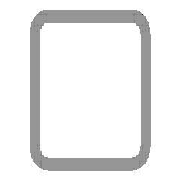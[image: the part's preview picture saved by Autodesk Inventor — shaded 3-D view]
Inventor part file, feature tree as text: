
AUTODESK INVENTOR PART (.ipt)
format: ipt  version: 2025 (Build 290162010, 162A)  size: 134,656 bytes
history: native  units: mm (DEFAULTED — no unit token found)
features: other x4, sketch x1, plane x1
ambient origin geometry x8: Origin, YZ Plane, XZ Plane, XY Plane, X Axis, Y Axis, Z Axis, Center Point
bodies: Solid1 (feature_tree), Body (feature_tree)
feature tree (6):
  parser-record x1  (decoder bookkeeping rows leaked as tree rows — omitted from the tree; the rows remain in map.json)
  other  "Driven Length"
  other  "Start Plane"
  other  "End Plane"
  sketch  "Sketch3"  dims[d3=2200.0mm d4=0.0mm d7=6.0mm d9=100.0mm d11=100.0mm d12=3.0mm d13=-0.0mm d14=2200.0mm d15=50.0mm d16=50.0mm d17=90.0deg d18=2200.0mm]
  plane  "Work Plane3"
